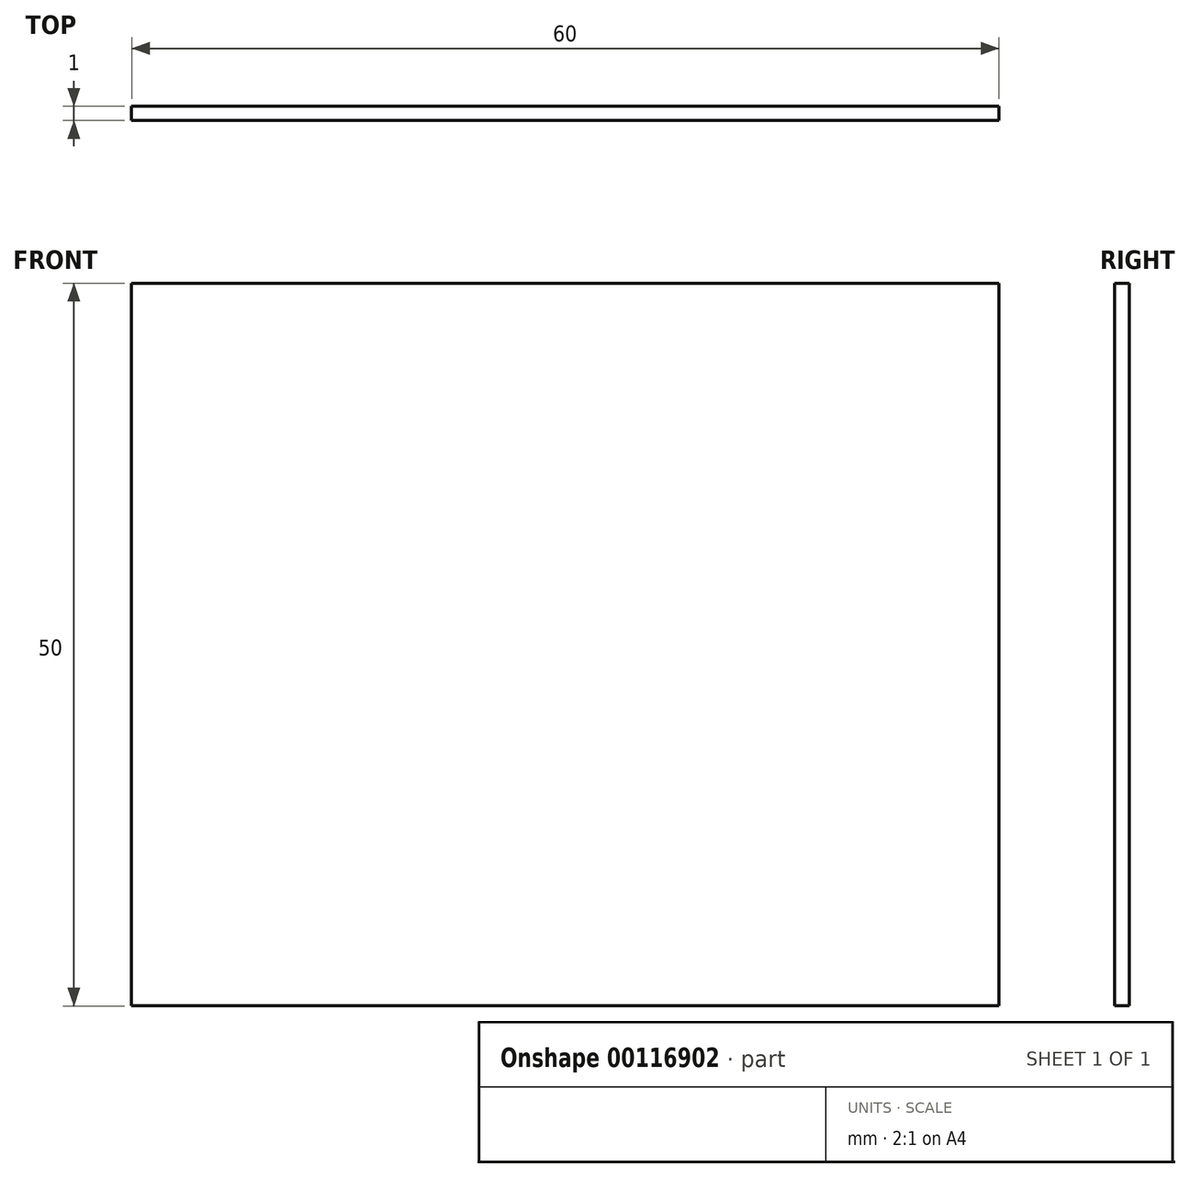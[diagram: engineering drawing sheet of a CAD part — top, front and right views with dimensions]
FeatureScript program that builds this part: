
annotation { "Feature Type Name" : "Feature", "Feature Type Description" : "" }
export const myFeature = defineFeature(function(context is Context, id is Id, definition is map)
    precondition{}
    {
        {
            var Q0;
            Q0=qCreatedBy(makeId("Front.planeOp"),FACE);
            var sketch = newSketch(context, id + "F0", { "sketchPlane" : qUnion([Q0])});
            skLineSegment(sketch, "E0.bottom", {"start": v(-53.01, 52.02) * mm, "end": v(6.99, 52.02) * mm});
            skLineSegment(sketch, "E0.top", {"start": v(-53.01, 2.02) * mm, "end": v(6.99, 2.02) * mm});
            skLineSegment(sketch, "E0.left", {"start": v(-53.01, 52.02) * mm, "end": v(-53.01, 2.02) * mm});
            skLineSegment(sketch, "E0.right", {"start": v(6.99, 52.02) * mm, "end": v(6.99, 2.02) * mm});
            skSolve(sketch);
        }
        {
            var Q0;
            Q0=makeQuery(id+"F0.imprint","IMPRINT",FACE,{"disambiguationData":[TD([[makeQuery(id+"F0.imprint","IMPRINT",EDGE,{"derivedFrom":sQuery(id+"F0.wireOp",EDGE,"E0.bottom")}),-1.0]])]});
            extrude(context, id + "F1", {"entities" : qUnion([Q0]), "depth" : 1 * mm});
        }
    });
